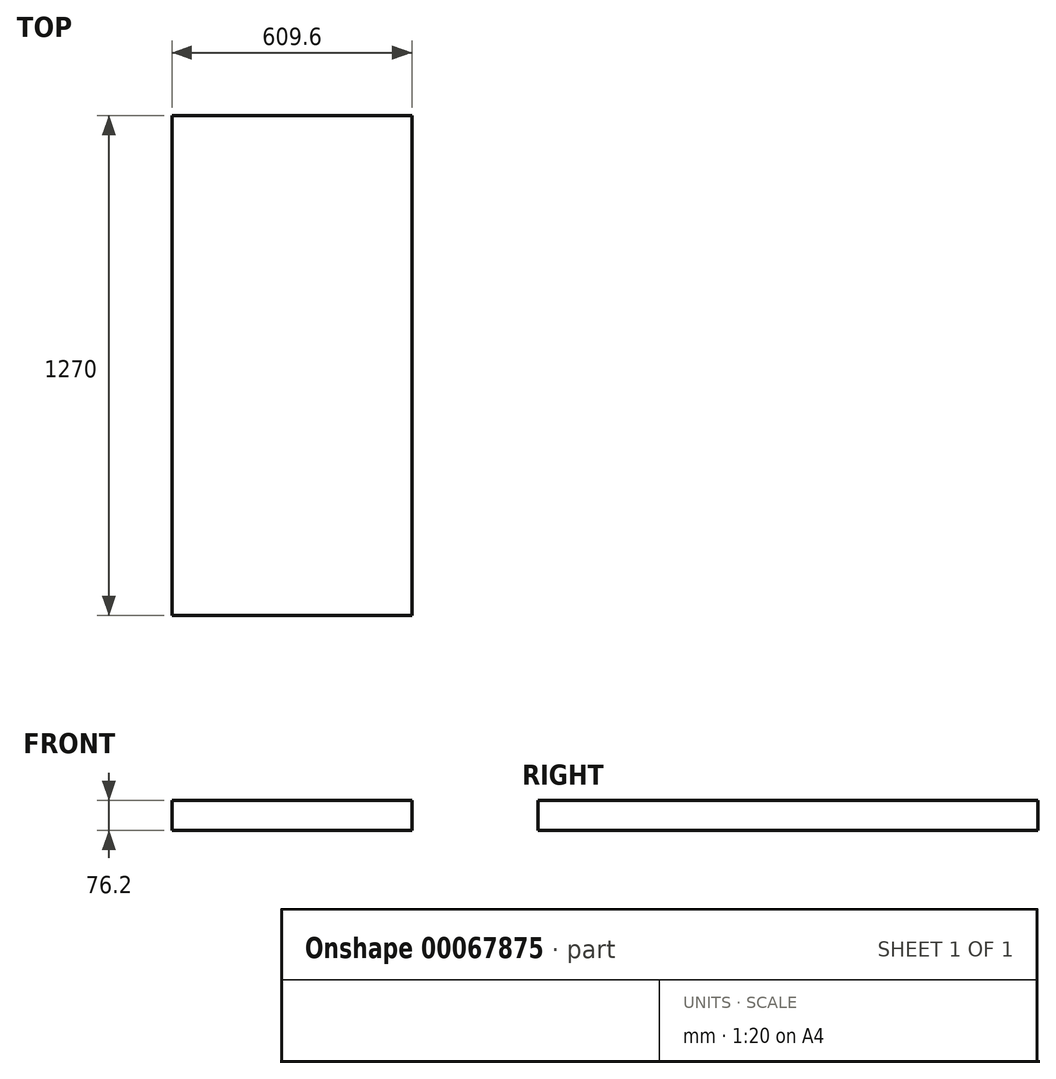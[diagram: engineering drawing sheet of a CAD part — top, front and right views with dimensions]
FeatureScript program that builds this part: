
annotation { "Feature Type Name" : "Feature", "Feature Type Description" : "" }
export const myFeature = defineFeature(function(context is Context, id is Id, definition is map)
    precondition{}
    {
        {
            var Q0;
            Q0=qCreatedBy(makeId("Top.planeOp"),FACE);
            var sketch = newSketch(context, id + "F0", { "sketchPlane" : qUnion([Q0])});
            skLineSegment(sketch, "E0.bottom", {"start": v(0, 0) * mm, "end": v(609.6, 0) * mm});
            skLineSegment(sketch, "E0.top", {"start": v(0, 1270) * mm, "end": v(609.6, 1270) * mm});
            skLineSegment(sketch, "E0.left", {"start": v(0, 0) * mm, "end": v(0, 1270) * mm});
            skLineSegment(sketch, "E0.right", {"start": v(609.6, 0) * mm, "end": v(609.6, 1270) * mm});
            skSolve(sketch);
        }
        {
            var Q0;
            Q0=makeQuery(id+"F0.imprint","IMPRINT",FACE,{"disambiguationData":[TD([[makeQuery(id+"F0.imprint","IMPRINT",EDGE,{"derivedFrom":sQuery(id+"F0.wireOp",EDGE,"E0.bottom")}),1.0]])]});
            extrude(context, id + "F1", {"entities" : qUnion([Q0]), "depth" : 76.2 * mm});
        }
    });
